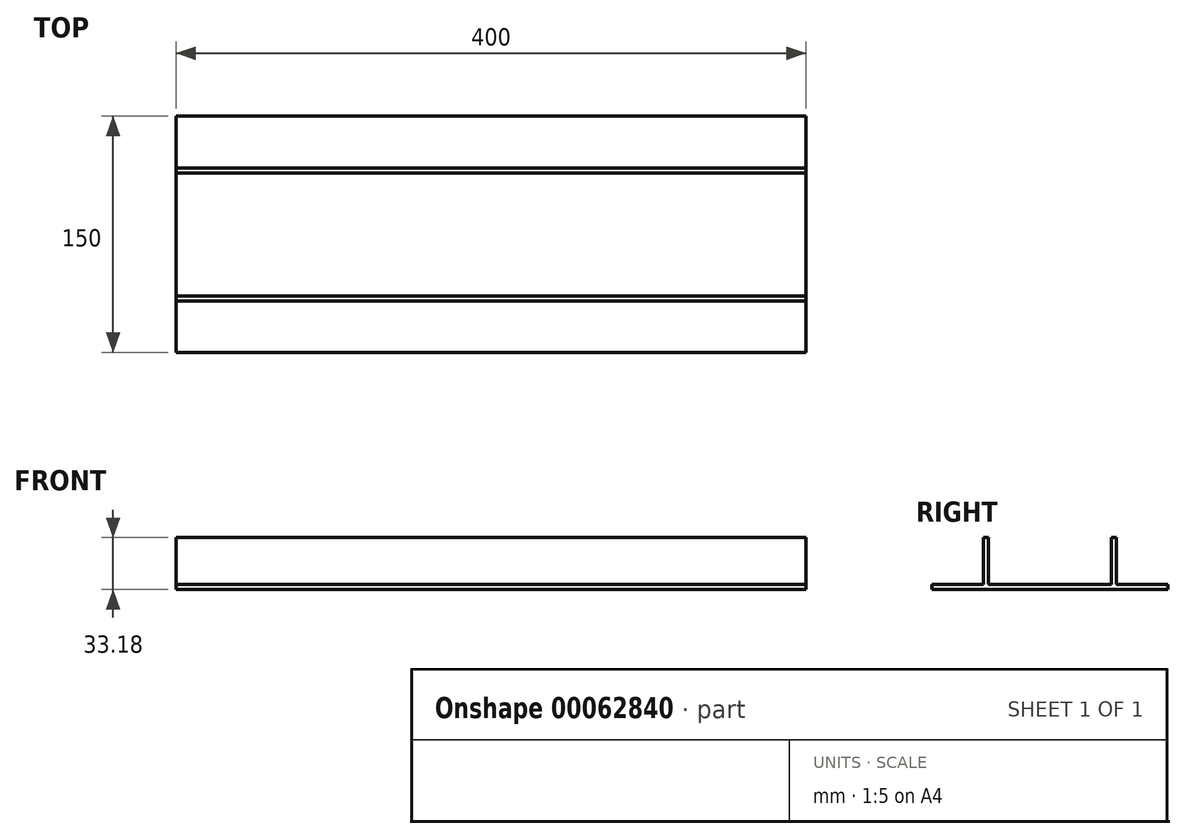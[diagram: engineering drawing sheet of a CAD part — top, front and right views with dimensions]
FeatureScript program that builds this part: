
annotation { "Feature Type Name" : "Feature", "Feature Type Description" : "" }
export const myFeature = defineFeature(function(context is Context, id is Id, definition is map)
    precondition{}
    {
        {
            var Q0;
            Q0=qCreatedBy(makeId("Top.planeOp"),FACE);
            var sketch = newSketch(context, id + "F0", { "sketchPlane" : qUnion([Q0])});
            skLineSegment(sketch, "E0.rect.bottom", {"start": v(-200, 75) * mm, "end": v(200, 75) * mm});
            skLineSegment(sketch, "E0.rect.top", {"start": v(-200, -75) * mm, "end": v(200, -75) * mm});
            skLineSegment(sketch, "E0.rect.left", {"start": v(-200, 75) * mm, "end": v(-200, -75) * mm});
            skLineSegment(sketch, "E0.rect.right", {"start": v(200, 75) * mm, "end": v(200, -75) * mm});
            skPoint(sketch, "E0.rect.middle", {"position": v(0, 0) * mm});
            skSolve(sketch);
        }
        {
            var Q0;
            Q0=makeQuery(id+"F0.imprint","IMPRINT",FACE,{"disambiguationData":[TD([[makeQuery(id+"F0.imprint","IMPRINT",EDGE,{"derivedFrom":sQuery(id+"F0.wireOp",EDGE,"E0.rect.bottom")}),-1.0]])]});
            extrude(context, id + "F1", {"entities" : qUnion([Q0]), "endBound" : BoundingType.SYMMETRIC, "depth" : 3.17 * mm});
        }
        {
            var Q0;
            Q0=makeQuery(id+"F1.opExtrude","CAP_FACE",FACE,{"disambiguationData":[OSD([sQuery(id+"F0.wireOp",EDGE,"E0.rect.bottom"),sQuery(id+"F0.wireOp",EDGE,"E0.rect.top"),sQuery(id+"F0.wireOp",EDGE,"E0.rect.left"),sQuery(id+"F0.wireOp",EDGE,"E0.rect.right")])],"isStart":false});
            var sketch = newSketch(context, id + "F2", { "sketchPlane" : qUnion([Q0])});
            skLineSegment(sketch, "E1.bottom", {"start": v(200, 39.03) * mm, "end": v(-200, 39.03) * mm});
            skLineSegment(sketch, "E1.top", {"start": v(200, 42.2) * mm, "end": v(-200, 42.2) * mm});
            skLineSegment(sketch, "E1.left", {"start": v(200, 39.03) * mm, "end": v(200, 42.2) * mm});
            skLineSegment(sketch, "E1.right", {"start": v(-200, 39.03) * mm, "end": v(-200, 42.2) * mm});
            skSolve(sketch);
        }
        {
            var Q0;
            Q0 = qSketchRegion(id + "F2", true);
            extrude(context, id + "F3", {"entities" : qUnion([Q0]), "depth" : 30 * mm});
        }
        {
            var Q0;
            Q0=makeQuery(id+"F3.opExtrude","SWEPT_BODY",BODY,{"disambiguationData":[OSD([sQuery(id+"F2.wireOp",EDGE,"E1.bottom"),sQuery(id+"F2.wireOp",EDGE,"E1.top"),sQuery(id+"F2.wireOp",EDGE,"E1.left"),sQuery(id+"F2.wireOp",EDGE,"E1.right")])]});
            var Q1;
            Q1=qCreatedBy(makeId("Front.planeOp"),FACE);
            mirror(context, id + "F4", {"operationType" : NewBodyOperationType.ADD, "entities" : qUnion([Q0]), "mirrorPlane" : qUnion([Q1])});
        }
    });
